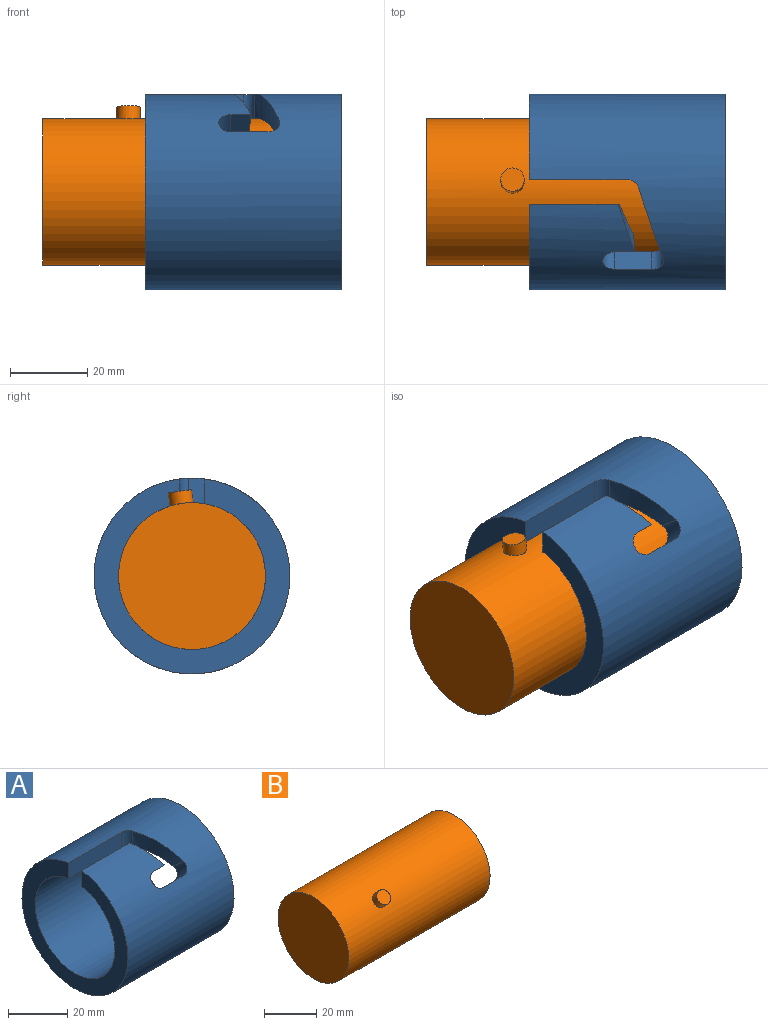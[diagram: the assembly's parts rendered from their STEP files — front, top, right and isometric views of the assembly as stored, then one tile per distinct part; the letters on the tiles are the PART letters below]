
ASSEMBLY  parts=2 mates=1
PART A: 13 faces, bbox 50.8x50.8x51.1 mm
  f0: cylinder r=19.05mm len=50.8mm, axis (-1,0,0), area 5745mm2, adj f2,f3,f4,f5,f6,f7,f8,f9
  f1: cylinder r=25.4mm len=50.8mm, axis (-1,0,0), area 7741.5mm2, adj f2,f3,f4,f5,f6,f7,f8,f9
  f2: plane 50.8x50.8mm, normal (1,0,0), area 886.7mm2, adj f0,f1
  f3: plane 50.8x50.6mm, normal (-1,0,0), area 846.3mm2, adj f0,f1,f5,f6
  f4: cylinder r=3.17mm len=6.6mm, axis (0,0,-1), area 25.6mm2, adj f0,f1,f5,f12
  f5: plane 25.4x6.42mm, normal (0,-1,0), area 163mm2, adj f0,f1,f3,f4
  f6: plane 23.31x6.42mm, normal (0,1,0), area 148.7mm2, adj f0,f1,f3,f11
  f7: cylinder r=3.17mm len=8.01mm, axis (0,0.71,-0.71), area 39.9mm2, adj f0,f1,f8,f12
  f8: plane 9.53x4.54mm, normal (0,0.71,0.71), area 61.1mm2, adj f0,f1,f7,f9
  f9: cylinder r=3.17mm len=9.17mm, axis (0,0.71,-0.71), area 63.7mm2, adj f0,f1,f8,f10
  f10: plane 5.17x4.54mm, normal (0,-0.71,-0.71), area 31.9mm2, adj f0,f1,f9,f11
  f11: bspline ~21.52x18.75mm, area 74.9mm2, adj f0,f1,f6,f10
  f12: bspline ~22.48x17.34mm, area 116.1mm2, adj f0,f1,f4,f7
PART B: 5 faces, bbox 76.2x38.1x38.1 mm
  f0: cylinder r=19.05mm len=76.2mm, axis (-1,0,0), area 9091.4mm2, adj f1,f2,f4
  f1: plane 38.1x38.1mm, normal (1,0,0), area 1140.1mm2, adj f0
  f2: plane 38.1x38.1mm, normal (-1,0,0), area 1140.1mm2, adj f0
  f3: plane 6.1x4.31mm, normal (0,-0.71,0.71), area 29.2mm2, adj f4
  f4: cylinder r=3.05mm len=6.73mm, axis (0,-0.71,0.71), area 63.2mm2, adj f0,f3
PLACE A at identity fixed
PLACE B rot(axis=(-1,0,0),53.2deg) t=(-26.58,0,0)mm
MATE cylindrical B.f0 <-> A.f0  axis (-1,0,0) through (11.52,0,0)mm
